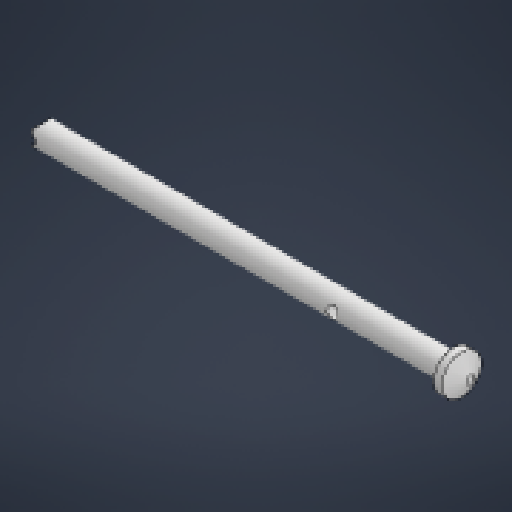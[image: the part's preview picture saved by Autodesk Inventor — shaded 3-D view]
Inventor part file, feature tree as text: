
AUTODESK INVENTOR PART (.ipt)
format: ipt  version: 2025.3 (Build 293356000, 356)  size: 146,432 bytes
history: native  units: mm
features: sketch x1, revolve x1, extrude x1
ambient origin geometry x8: Origin, YZ Plane, XZ Plane, XY Plane, X Axis, Y Axis, Z Axis, Center Point
bodies: Solid1 (feature_tree)
feature tree (3):
  sketch  "Sketch1"  dims[d0=6.0mm d1=3.0mm d2=60.0deg d3=2.0mm d4=10.0mm d5=2.0mm d6=110.0mm d7=360.0deg d8=0.0mm d9=0.0mm d10=3.0mm d14=2.5mm d16=31.98mm d13=0.872665mm]
  revolve  "Revolution1"  [1 undecoded]
  extrude  "Extrusion1"  TaperAngle=60.0deg  [1 undecoded]
note: 2 required parameter values undecoded (feature->parameter linkage not recoverable at this tier; creation-order binding heuristic only, values carry confidence <= 0.55)